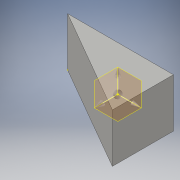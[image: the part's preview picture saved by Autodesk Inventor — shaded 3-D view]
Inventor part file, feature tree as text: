
AUTODESK INVENTOR PART (.ipt)
format: ipt  version: 2016 (Build 200138000, 138)  size: 91,136 bytes
history: native  units: in
note: dims shown in document units (in); Inventor stores cm internally (conversion verified against a paired STEP export)
features: sketch x2, extrude x1
ambient origin geometry x8: Origin, YZ Plane, XZ Plane, XY Plane, X Axis, Y Axis, Z Axis, Center Point
bodies: Body1 (feature_tree)
feature tree (3):
  extrude  "Extrusion2"  TaperAngle=150.0deg  [1 undecoded]
  sketch  "Sketch3"  dims[d6=7.874in d7=0.0in]
  sketch  "Sketch2"  dims[d4=19.685in d5=150.0deg]
note: 1 required parameter value undecoded (feature->parameter linkage not recoverable at this tier; creation-order binding heuristic only, values carry confidence <= 0.55)
